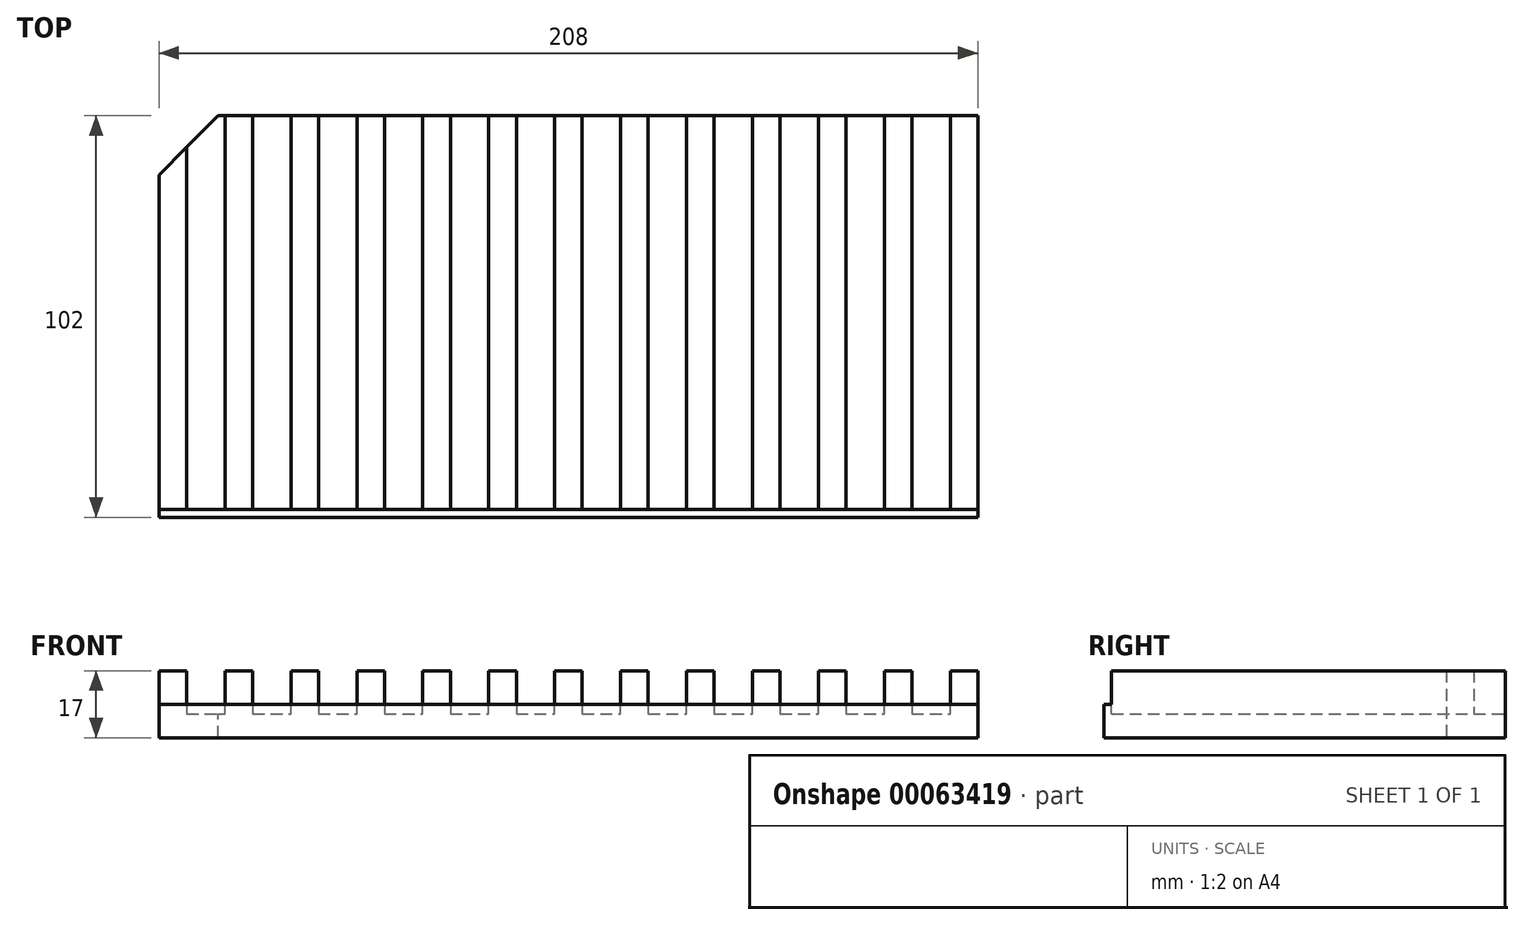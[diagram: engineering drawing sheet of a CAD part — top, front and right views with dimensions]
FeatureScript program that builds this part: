
annotation { "Feature Type Name" : "Feature", "Feature Type Description" : "" }
export const myFeature = defineFeature(function(context is Context, id is Id, definition is map)
    precondition{}
    {
        {
            var Q0;
            Q0=qCreatedBy(makeId("Front.planeOp"),FACE);
            var sketch = newSketch(context, id + "F0", { "sketchPlane" : qUnion([Q0])});
            skLineSegment(sketch, "E0", {"start": v(0, 0) * mm, "end": v(7, 0) * mm});
            skLineSegment(sketch, "E1", {"start": v(7, 0) * mm, "end": v(7, -11) * mm});
            skLineSegment(sketch, "E2", {"start": v(7, -11) * mm, "end": v(16.75, -11) * mm});
            skLineSegment(sketch, "E3", {"start": v(16.75, -11) * mm, "end": v(16.75, 0) * mm});
            skLineSegment(sketch, "E4.1.0.0", {"start": v(33.5, -11) * mm, "end": v(33.5, 0) * mm});
            skLineSegment(sketch, "E4.1.0.1", {"start": v(16.75, 0) * mm, "end": v(23.75, 0) * mm});
            skLineSegment(sketch, "E4.1.0.2", {"start": v(23.75, 0) * mm, "end": v(23.75, -11) * mm});
            skLineSegment(sketch, "E4.1.0.3", {"start": v(23.75, -11) * mm, "end": v(33.5, -11) * mm});
            skLineSegment(sketch, "E4.2.0.0", {"start": v(50.25, -11) * mm, "end": v(50.25, 0) * mm});
            skLineSegment(sketch, "E4.2.0.1", {"start": v(33.5, 0) * mm, "end": v(40.5, 0) * mm});
            skLineSegment(sketch, "E4.2.0.2", {"start": v(40.5, 0) * mm, "end": v(40.5, -11) * mm});
            skLineSegment(sketch, "E4.2.0.3", {"start": v(40.5, -11) * mm, "end": v(50.25, -11) * mm});
            skLineSegment(sketch, "E4.3.0.0", {"start": v(67, -11) * mm, "end": v(67, 0) * mm});
            skLineSegment(sketch, "E4.3.0.1", {"start": v(50.25, 0) * mm, "end": v(57.25, 0) * mm});
            skLineSegment(sketch, "E4.3.0.2", {"start": v(57.25, 0) * mm, "end": v(57.25, -11) * mm});
            skLineSegment(sketch, "E4.3.0.3", {"start": v(57.25, -11) * mm, "end": v(67, -11) * mm});
            skLineSegment(sketch, "E4.4.0.0", {"start": v(83.75, -11) * mm, "end": v(83.75, 0) * mm});
            skLineSegment(sketch, "E4.4.0.1", {"start": v(67, 0) * mm, "end": v(74, 0) * mm});
            skLineSegment(sketch, "E4.4.0.2", {"start": v(74, 0) * mm, "end": v(74, -11) * mm});
            skLineSegment(sketch, "E4.4.0.3", {"start": v(74, -11) * mm, "end": v(83.75, -11) * mm});
            skLineSegment(sketch, "E4.5.0.0", {"start": v(100.5, -11) * mm, "end": v(100.5, 0) * mm});
            skLineSegment(sketch, "E4.5.0.1", {"start": v(83.75, 0) * mm, "end": v(90.75, 0) * mm});
            skLineSegment(sketch, "E4.5.0.2", {"start": v(90.75, 0) * mm, "end": v(90.75, -11) * mm});
            skLineSegment(sketch, "E4.5.0.3", {"start": v(90.75, -11) * mm, "end": v(100.5, -11) * mm});
            skLineSegment(sketch, "E4.6.0.0", {"start": v(117.25, -11) * mm, "end": v(117.25, 0) * mm});
            skLineSegment(sketch, "E4.6.0.1", {"start": v(100.5, 0) * mm, "end": v(107.5, 0) * mm});
            skLineSegment(sketch, "E4.6.0.2", {"start": v(107.5, 0) * mm, "end": v(107.5, -11) * mm});
            skLineSegment(sketch, "E4.6.0.3", {"start": v(107.5, -11) * mm, "end": v(117.25, -11) * mm});
            skLineSegment(sketch, "E4.7.0.0", {"start": v(134, -11) * mm, "end": v(134, 0) * mm});
            skLineSegment(sketch, "E4.7.0.1", {"start": v(117.25, 0) * mm, "end": v(124.25, 0) * mm});
            skLineSegment(sketch, "E4.7.0.2", {"start": v(124.25, 0) * mm, "end": v(124.25, -11) * mm});
            skLineSegment(sketch, "E4.7.0.3", {"start": v(124.25, -11) * mm, "end": v(134, -11) * mm});
            skLineSegment(sketch, "E4.8.0.0", {"start": v(150.75, -11) * mm, "end": v(150.75, 0) * mm});
            skLineSegment(sketch, "E4.8.0.1", {"start": v(134, 0) * mm, "end": v(141, 0) * mm});
            skLineSegment(sketch, "E4.8.0.2", {"start": v(141, 0) * mm, "end": v(141, -11) * mm});
            skLineSegment(sketch, "E4.8.0.3", {"start": v(141, -11) * mm, "end": v(150.75, -11) * mm});
            skLineSegment(sketch, "E4.9.0.0", {"start": v(167.5, -11) * mm, "end": v(167.5, 0) * mm});
            skLineSegment(sketch, "E4.9.0.1", {"start": v(150.75, 0) * mm, "end": v(157.75, 0) * mm});
            skLineSegment(sketch, "E4.9.0.2", {"start": v(157.75, 0) * mm, "end": v(157.75, -11) * mm});
            skLineSegment(sketch, "E4.9.0.3", {"start": v(157.75, -11) * mm, "end": v(167.5, -11) * mm});
            skLineSegment(sketch, "E4.10.0.0", {"start": v(184.25, -11) * mm, "end": v(184.25, 0) * mm});
            skLineSegment(sketch, "E4.10.0.1", {"start": v(167.5, 0) * mm, "end": v(174.5, 0) * mm});
            skLineSegment(sketch, "E4.10.0.2", {"start": v(174.5, 0) * mm, "end": v(174.5, -11) * mm});
            skLineSegment(sketch, "E4.10.0.3", {"start": v(174.5, -11) * mm, "end": v(184.25, -11) * mm});
            skLineSegment(sketch, "E4.11.0.0", {"start": v(201, -11) * mm, "end": v(201, 0) * mm});
            skLineSegment(sketch, "E4.11.0.1", {"start": v(184.25, 0) * mm, "end": v(191.25, 0) * mm});
            skLineSegment(sketch, "E4.11.0.2", {"start": v(191.25, 0) * mm, "end": v(191.25, -11) * mm});
            skLineSegment(sketch, "E4.11.0.3", {"start": v(191.25, -11) * mm, "end": v(201, -11) * mm});
            skLineSegment(sketch, "E4.direction1", {"start": v(7, -11) * mm, "end": v(23.75, -11) * mm, "construction": true});
            skLineSegment(sketch, "E5", {"start": v(0, 0) * mm, "end": v(0, -17) * mm});
            skLineSegment(sketch, "E6", {"start": v(0, -17) * mm, "end": v(208, -17) * mm});
            skLineSegment(sketch, "E7", {"start": v(208, -17) * mm, "end": v(208, 0) * mm});
            skLineSegment(sketch, "E8", {"start": v(208, 0) * mm, "end": v(201, 0) * mm});
            skSolve(sketch);
        }
        {
            var Q0;
            Q0 = qSketchRegion(id + "F0", true);
            extrude(context, id + "F1", {"entities" : qUnion([Q0]), "depth" : 100 * mm});
        }
        {
            var Q0;
            Q0=makeQuery(id+"F1.opExtrude","CAP_EDGE",EDGE,{"disambiguationData":[OSD([sQuery(id+"F0.wireOp",EDGE,"E5")])],"isStart":true});
            chamfer(context, id + "F2", {"entities" : qUnion([Q0]), "chamferType" : ChamferType.OFFSET_ANGLE, "width" : 15 * mm, "oppositeDirection" : false, "angle" : 45 * degree, "tangentPropagation" : true});
        }
        {
            var Q0;
            Q0=makeQuery(id+"F1.opExtrude","CAP_FACE",FACE,{"disambiguationData":[OSD([sQuery(id+"F0.wireOp",EDGE,"E0"),sQuery(id+"F0.wireOp",EDGE,"E1"),sQuery(id+"F0.wireOp",EDGE,"E2"),sQuery(id+"F0.wireOp",EDGE,"E3"),sQuery(id+"F0.wireOp",EDGE,"E4.1.0.0"),sQuery(id+"F0.wireOp",EDGE,"E4.1.0.1"),sQuery(id+"F0.wireOp",EDGE,"E4.1.0.2"),sQuery(id+"F0.wireOp",EDGE,"E4.1.0.3"),sQuery(id+"F0.wireOp",EDGE,"E4.2.0.0"),sQuery(id+"F0.wireOp",EDGE,"E4.2.0.1"),sQuery(id+"F0.wireOp",EDGE,"E4.2.0.2"),sQuery(id+"F0.wireOp",EDGE,"E4.2.0.3"),sQuery(id+"F0.wireOp",EDGE,"E4.3.0.0"),sQuery(id+"F0.wireOp",EDGE,"E4.3.0.1"),sQuery(id+"F0.wireOp",EDGE,"E4.3.0.2"),sQuery(id+"F0.wireOp",EDGE,"E4.3.0.3"),sQuery(id+"F0.wireOp",EDGE,"E4.4.0.0"),sQuery(id+"F0.wireOp",EDGE,"E4.4.0.1"),sQuery(id+"F0.wireOp",EDGE,"E4.4.0.2"),sQuery(id+"F0.wireOp",EDGE,"E4.4.0.3"),sQuery(id+"F0.wireOp",EDGE,"E4.5.0.0"),sQuery(id+"F0.wireOp",EDGE,"E4.5.0.1"),sQuery(id+"F0.wireOp",EDGE,"E4.5.0.2"),sQuery(id+"F0.wireOp",EDGE,"E4.5.0.3"),sQuery(id+"F0.wireOp",EDGE,"E4.6.0.0"),sQuery(id+"F0.wireOp",EDGE,"E4.6.0.1"),sQuery(id+"F0.wireOp",EDGE,"E4.6.0.2"),sQuery(id+"F0.wireOp",EDGE,"E4.6.0.3"),sQuery(id+"F0.wireOp",EDGE,"E4.7.0.0"),sQuery(id+"F0.wireOp",EDGE,"E4.7.0.1"),sQuery(id+"F0.wireOp",EDGE,"E4.7.0.2"),sQuery(id+"F0.wireOp",EDGE,"E4.7.0.3"),sQuery(id+"F0.wireOp",EDGE,"E4.8.0.0"),sQuery(id+"F0.wireOp",EDGE,"E4.8.0.1"),sQuery(id+"F0.wireOp",EDGE,"E4.8.0.2"),sQuery(id+"F0.wireOp",EDGE,"E4.8.0.3"),sQuery(id+"F0.wireOp",EDGE,"E4.9.0.0"),sQuery(id+"F0.wireOp",EDGE,"E4.9.0.1"),sQuery(id+"F0.wireOp",EDGE,"E4.9.0.2"),sQuery(id+"F0.wireOp",EDGE,"E4.9.0.3"),sQuery(id+"F0.wireOp",EDGE,"E4.10.0.0"),sQuery(id+"F0.wireOp",EDGE,"E4.10.0.1"),sQuery(id+"F0.wireOp",EDGE,"E4.10.0.2"),sQuery(id+"F0.wireOp",EDGE,"E4.10.0.3"),sQuery(id+"F0.wireOp",EDGE,"E4.11.0.0"),sQuery(id+"F0.wireOp",EDGE,"E4.11.0.1"),sQuery(id+"F0.wireOp",EDGE,"E4.11.0.2"),sQuery(id+"F0.wireOp",EDGE,"E4.11.0.3"),sQuery(id+"F0.wireOp",EDGE,"E5"),sQuery(id+"F0.wireOp",EDGE,"E6"),sQuery(id+"F0.wireOp",EDGE,"E7"),sQuery(id+"F0.wireOp",EDGE,"E8")])],"isStart":false});
            var sketch = newSketch(context, id + "F3", { "sketchPlane" : qUnion([Q0])});
            skLineSegment(sketch, "E9.bottom", {"start": v(0, -17) * mm, "end": v(208, -17) * mm});
            skLineSegment(sketch, "E9.top", {"start": v(0, -8.5) * mm, "end": v(208, -8.5) * mm});
            skLineSegment(sketch, "E9.left", {"start": v(0, -17) * mm, "end": v(0, -8.5) * mm});
            skLineSegment(sketch, "E9.right", {"start": v(208, -17) * mm, "end": v(208, -8.5) * mm});
            skSolve(sketch);
        }
        {
            var Q0;
            Q0 = qSketchRegion(id + "F3", true);
            extrude(context, id + "F4", {"entities" : qUnion([Q0]), "operationType" : NewBodyOperationType.ADD, "depth" : 2 * mm});
        }
    });
